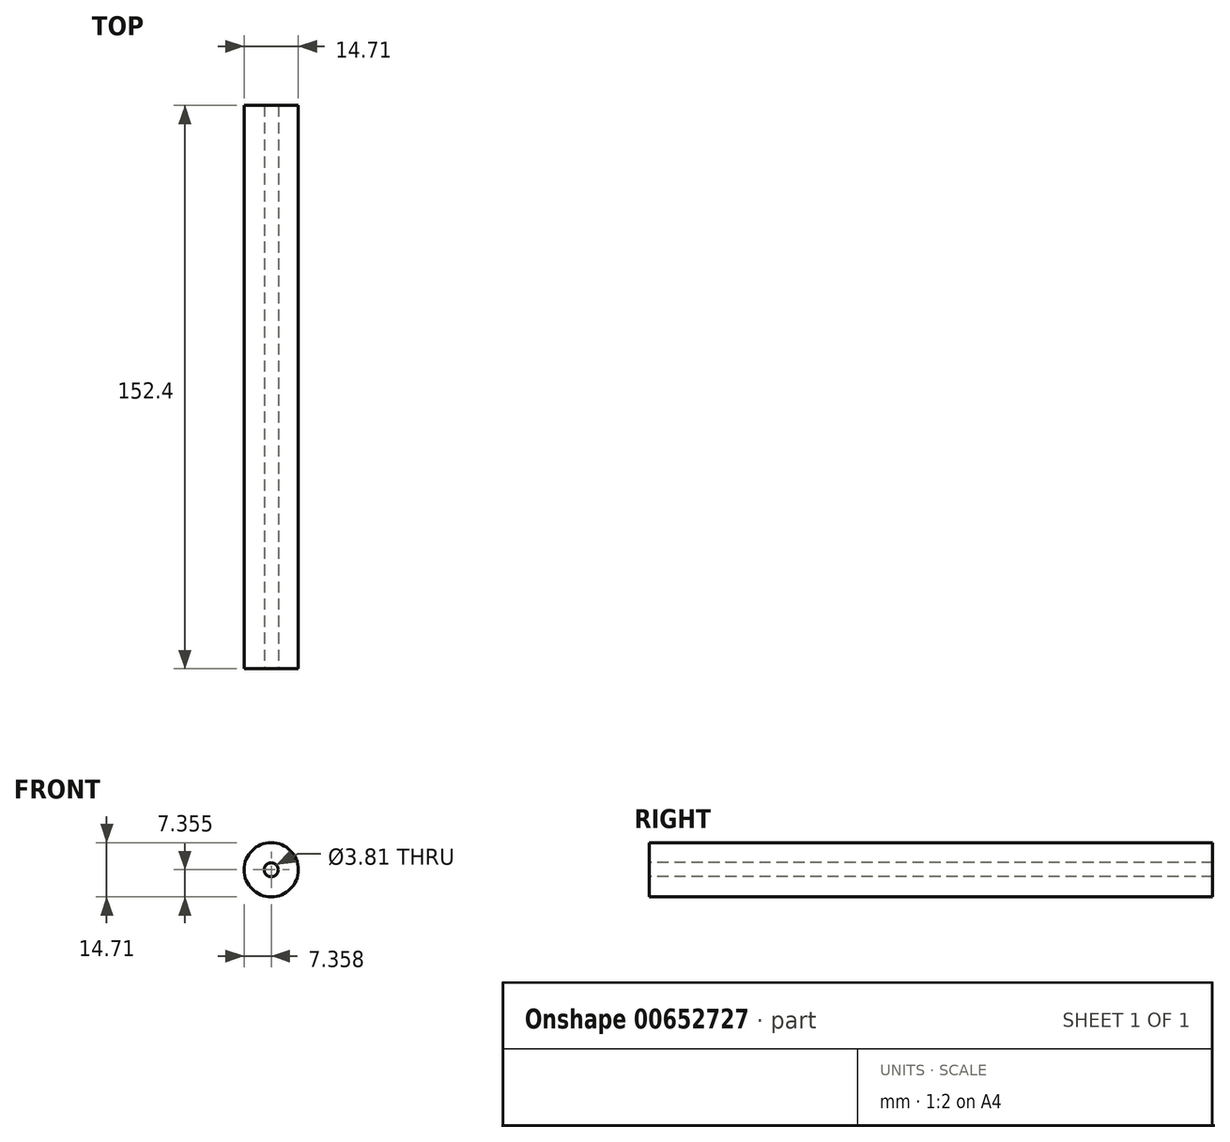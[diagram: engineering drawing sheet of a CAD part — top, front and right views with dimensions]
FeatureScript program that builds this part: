
annotation { "Feature Type Name" : "Feature", "Feature Type Description" : "" }
export const myFeature = defineFeature(function(context is Context, id is Id, definition is map)
    precondition{}
    {
        {
            var Q0;
            Q0=qCreatedBy(makeId("Front.planeOp"),FACE);
            var sketch = newSketch(context, id + "F0", { "sketchPlane" : qUnion([Q0])});
            skCircle(sketch, "E0", {"center": v(-44.14, 8.63) * mm, "radius": 7.35 * mm});
            skSolve(sketch);
        }
        {
            var Q0;
            Q0 = qSketchRegion(id + "F0", true);
            extrude(context, id + "F1", {"entities" : qUnion([Q0]), "depth" : 152.4 * mm, "offsetDistance" : 25.4 * mm});
        }
        {
            var Q0;
            Q0=sQuery(id+"F0.wireOp",VERTEX,"E0.center");
            var Q1;
            Q1=makeQuery(id+"F1.opExtrude","SWEPT_BODY",BODY,{"disambiguationData":[OSD([sQuery(id+"F0.wireOp",EDGE,"E0")])]});
            hole(context, id + "F2", {"style" : HoleStyle.SIMPLE, "endStyle" : HoleEndStyle.THROUGH, "oppositeDirection" : true, "holeDiameter" : 3.8 * mm, "majorDiameter" : 6.35 * mm, "isTappedThrough" : true, "tappedDepth" : 12.7 * mm, "tapClearance" : 3, "startFromSketch" : true, "locations" : qUnion([Q0]), "scope" : qUnion([Q1])});
        }
    });
